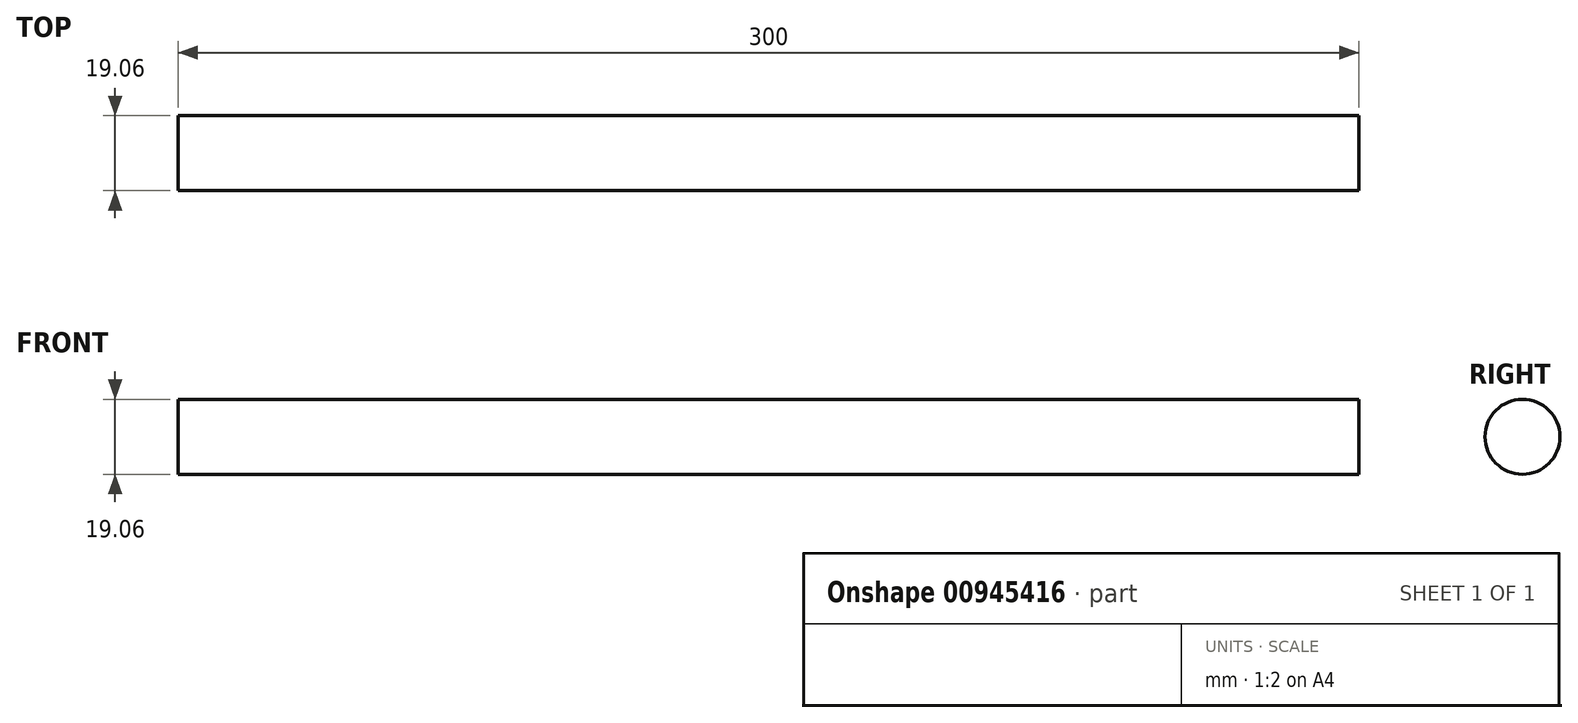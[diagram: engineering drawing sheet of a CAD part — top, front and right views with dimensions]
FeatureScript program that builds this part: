
annotation { "Feature Type Name" : "Feature", "Feature Type Description" : "" }
export const myFeature = defineFeature(function(context is Context, id is Id, definition is map)
    precondition{}
    {
        {
            var Q0;
            Q0=qCreatedBy(makeId("Right.planeOp"),FACE);
            var sketch = newSketch(context, id + "F0", { "sketchPlane" : qUnion([Q0])});
            skCircle(sketch, "E0", {"center": v(0, 0) * mm, "radius": 9.53 * mm});
            skSolve(sketch);
        }
        {
            var Q0;
            Q0=sQuery(id+"F0.wireOp",EDGE,"E0");
            extrude(context, id + "F1", {"bodyType" : ToolBodyType.SURFACE, "surfaceEntities" : qUnion([Q0]), "depth" : 300 * mm, "offsetDistance" : 25.4 * mm});
        }
    });
